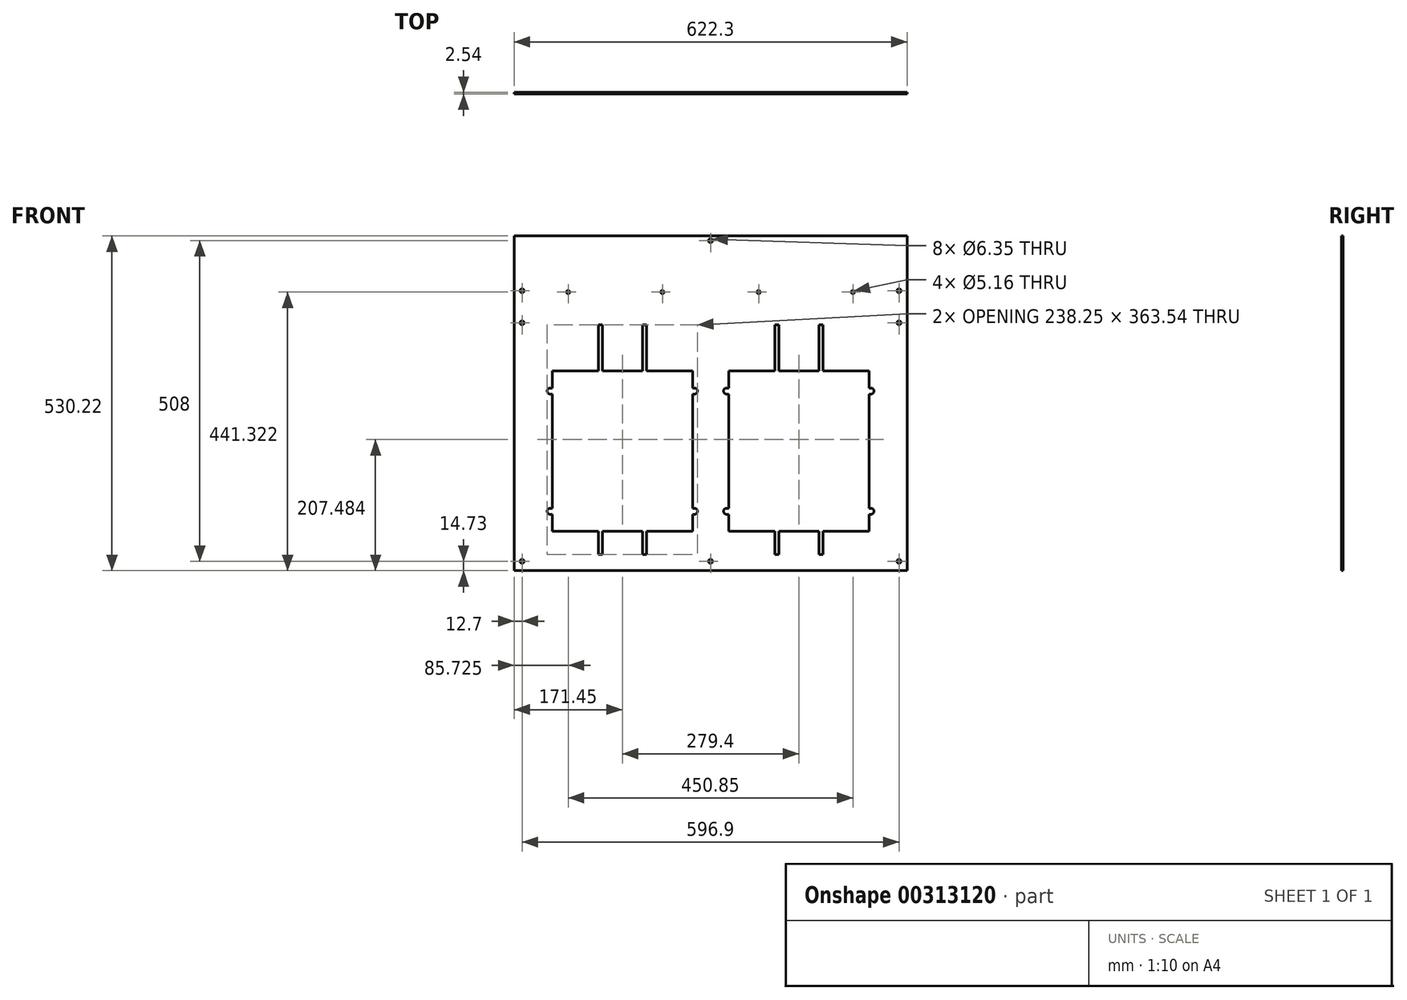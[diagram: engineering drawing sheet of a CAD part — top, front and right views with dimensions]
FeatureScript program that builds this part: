
annotation { "Feature Type Name" : "Feature", "Feature Type Description" : "" }
export const myFeature = defineFeature(function(context is Context, id is Id, definition is map)
    precondition{}
    {
        {
            var Q0;
            Q0=qCreatedBy(makeId("Front.planeOp"),FACE);
            var sketch = newSketch(context, id + "F0", { "sketchPlane" : qUnion([Q0])});
            skLineSegment(sketch, "E0.bottom", {"start": v(-311.15, 265.11) * mm, "end": v(311.15, 265.11) * mm});
            skLineSegment(sketch, "E0.top", {"start": v(-311.15, -265.11) * mm, "end": v(311.15, -265.11) * mm});
            skLineSegment(sketch, "E0.left", {"start": v(-311.15, 265.11) * mm, "end": v(-311.15, -265.11) * mm});
            skLineSegment(sketch, "E0.right", {"start": v(311.15, 265.11) * mm, "end": v(311.15, -265.11) * mm});
            skLineSegment(sketch, "E1.bottom", {"start": v(-250.83, 51.12) * mm, "end": v(-28.57, 51.12) * mm});
            skLineSegment(sketch, "E1.top", {"start": v(-250.82, -202.88) * mm, "end": v(-28.57, -202.88) * mm});
            skLineSegment(sketch, "E1.left", {"start": v(-250.82, 51.12) * mm, "end": v(-250.82, 24.2) * mm});
            skLineSegment(sketch, "E1.right", {"start": v(-28.57, 51.12) * mm, "end": v(-28.57, 24.2) * mm});
            skPoint(sketch, "E1.middle", {"position": v(-139.7, -75.88) * mm});
            skLineSegment(sketch, "E2", {"start": v(0, -75.88) * mm, "end": v(0, 0) * mm, "construction": true});
            skLineSegment(sketch, "E3", {"start": v(-139.7, -75.88) * mm, "end": v(0, -75.88) * mm, "construction": true});
            skArc(sketch, "E4", {"start": v(-254, 24.2) * mm, "mid": v(-258.83, 19.37) * mm, "end": v(-254, 14.54) * mm});
            skArc(sketch, "E5", {"start": v(-25.4, 14.54) * mm, "mid": v(-20.57, 19.37) * mm, "end": v(-25.4, 24.2) * mm});
            skArc(sketch, "E6", {"start": v(-25.4, -175.96) * mm, "mid": v(-20.57, -171.13) * mm, "end": v(-25.4, -166.3) * mm});
            skArc(sketch, "E7", {"start": v(-254, -166.3) * mm, "mid": v(-258.83, -171.13) * mm, "end": v(-254, -175.96) * mm});
            skLineSegment(sketch, "E8", {"start": v(-25.4, 24.2) * mm, "end": v(-28.58, 24.2) * mm});
            skLineSegment(sketch, "E9", {"start": v(-25.4, 14.54) * mm, "end": v(-28.57, 14.54) * mm});
            skLineSegment(sketch, "E10.trimOffspring", {"start": v(-28.57, 14.54) * mm, "end": v(-28.57, -166.3) * mm});
            skLineSegment(sketch, "E11", {"start": v(-25.4, -166.3) * mm, "end": v(-28.57, -166.3) * mm});
            skLineSegment(sketch, "E12", {"start": v(-25.4, -175.96) * mm, "end": v(-28.57, -175.96) * mm});
            skLineSegment(sketch, "E13.trimOffspring", {"start": v(-28.57, -175.96) * mm, "end": v(-28.57, -202.88) * mm});
            skLineSegment(sketch, "E14", {"start": v(-254, -166.3) * mm, "end": v(-250.82, -166.3) * mm});
            skLineSegment(sketch, "E15", {"start": v(-254, -175.96) * mm, "end": v(-250.82, -175.96) * mm});
            skLineSegment(sketch, "E16", {"start": v(-254, 24.2) * mm, "end": v(-250.82, 24.2) * mm});
            skLineSegment(sketch, "E17", {"start": v(-254, 14.54) * mm, "end": v(-250.82, 14.54) * mm});
            skLineSegment(sketch, "E18.trimOffspring", {"start": v(-250.82, 14.54) * mm, "end": v(-250.82, -166.3) * mm});
            skLineSegment(sketch, "E19.trimOffspring", {"start": v(-250.82, -175.96) * mm, "end": v(-250.82, -202.88) * mm});
            skLineSegment(sketch, "E20.1.0.0", {"start": v(28.57, -175.96) * mm, "end": v(28.57, -202.88) * mm});
            skLineSegment(sketch, "E20.1.0.1", {"start": v(250.82, 14.54) * mm, "end": v(250.82, -166.3) * mm});
            skLineSegment(sketch, "E20.1.0.2", {"start": v(139.7, -75.88) * mm, "end": v(279.4, -75.88) * mm, "construction": true});
            skLineSegment(sketch, "E20.1.0.3", {"start": v(250.82, 51.12) * mm, "end": v(250.82, 24.2) * mm});
            skLineSegment(sketch, "E20.1.0.4", {"start": v(250.82, -175.96) * mm, "end": v(250.82, -202.88) * mm});
            skPoint(sketch, "E20.1.0.5", {"position": v(139.7, -75.88) * mm});
            skLineSegment(sketch, "E20.1.0.6", {"start": v(28.57, 51.12) * mm, "end": v(250.82, 51.12) * mm});
            skLineSegment(sketch, "E20.1.0.7", {"start": v(28.57, -202.88) * mm, "end": v(250.82, -202.88) * mm});
            skLineSegment(sketch, "E20.1.0.8", {"start": v(28.57, 14.54) * mm, "end": v(28.57, -166.3) * mm});
            skLineSegment(sketch, "E20.1.0.9", {"start": v(28.57, 51.12) * mm, "end": v(28.57, 24.2) * mm});
            skLineSegment(sketch, "E20.1.0.10", {"start": v(25.4, -166.3) * mm, "end": v(28.57, -166.3) * mm});
            skLineSegment(sketch, "E20.1.0.11", {"start": v(25.4, 24.2) * mm, "end": v(28.58, 24.2) * mm});
            skArc(sketch, "E20.1.0.12", {"start": v(254, -175.96) * mm, "mid": v(258.83, -171.13) * mm, "end": v(254, -166.3) * mm});
            skLineSegment(sketch, "E20.1.0.13", {"start": v(254, -175.96) * mm, "end": v(250.82, -175.96) * mm});
            skLineSegment(sketch, "E20.1.0.14", {"start": v(25.4, -175.96) * mm, "end": v(28.57, -175.96) * mm});
            skLineSegment(sketch, "E20.1.0.15", {"start": v(254, -166.3) * mm, "end": v(250.82, -166.3) * mm});
            skArc(sketch, "E20.1.0.16", {"start": v(25.4, -166.3) * mm, "mid": v(20.57, -171.13) * mm, "end": v(25.4, -175.96) * mm});
            skLineSegment(sketch, "E20.1.0.17", {"start": v(254, 24.2) * mm, "end": v(250.82, 24.2) * mm});
            skLineSegment(sketch, "E20.1.0.18", {"start": v(254, 14.54) * mm, "end": v(250.82, 14.54) * mm});
            skArc(sketch, "E20.1.0.19", {"start": v(254, 14.54) * mm, "mid": v(258.83, 19.37) * mm, "end": v(254, 24.2) * mm});
            skLineSegment(sketch, "E20.1.0.20", {"start": v(25.4, 14.54) * mm, "end": v(28.57, 14.54) * mm});
            skArc(sketch, "E20.1.0.21", {"start": v(25.4, 24.2) * mm, "mid": v(20.57, 19.37) * mm, "end": v(25.4, 14.54) * mm});
            skLineSegment(sketch, "E20.direction1", {"start": v(-250.82, -202.88) * mm, "end": v(28.57, -202.88) * mm, "construction": true});
            skCircle(sketch, "E21", {"center": v(0, 257.62) * mm, "radius": 3.18 * mm});
            skCircle(sketch, "E22", {"center": v(-298.45, 178.24) * mm, "radius": 3.18 * mm});
            skCircle(sketch, "E23", {"center": v(-298.45, 127.44) * mm, "radius": 3.18 * mm});
            skCircle(sketch, "E24", {"center": v(-298.45, -250.38) * mm, "radius": 3.17 * mm});
            skCircle(sketch, "E25", {"center": v(298.45, 178.24) * mm, "radius": 3.18 * mm});
            skCircle(sketch, "E26", {"center": v(298.45, 127.44) * mm, "radius": 3.18 * mm});
            skCircle(sketch, "E27", {"center": v(298.45, -250.38) * mm, "radius": 3.18 * mm});
            skCircle(sketch, "E28", {"center": v(0, -250.38) * mm, "radius": 3.18 * mm});
            skPoint(sketch, "E28.centerSnap0", {"position": v(0, -265.11) * mm});
            skSolve(sketch);
        }
        {
            var Q0;
            Q0 = qSketchRegion(id + "F0", true);
            extrude(context, id + "F1", {"entities" : qUnion([Q0]), "endBound" : BoundingType.SYMMETRIC, "depth" : 2.54 * mm});
        }
        {
            var Q0;
            Q0=makeQuery(id+"F1.opExtrude","CAP_FACE",FACE,{"disambiguationData":[OSD([sQuery(id+"F0.wireOp",EDGE,"E0.bottom"),sQuery(id+"F0.wireOp",EDGE,"E0.top"),sQuery(id+"F0.wireOp",EDGE,"E0.left"),sQuery(id+"F0.wireOp",EDGE,"E0.right"),sQuery(id+"F0.wireOp",EDGE,"E1.bottom"),sQuery(id+"F0.wireOp",EDGE,"E1.top"),sQuery(id+"F0.wireOp",EDGE,"E1.left"),sQuery(id+"F0.wireOp",EDGE,"E1.right"),sQuery(id+"F0.wireOp",EDGE,"E4"),sQuery(id+"F0.wireOp",EDGE,"E5"),sQuery(id+"F0.wireOp",EDGE,"E6"),sQuery(id+"F0.wireOp",EDGE,"E7"),sQuery(id+"F0.wireOp",EDGE,"E8"),sQuery(id+"F0.wireOp",EDGE,"E9"),sQuery(id+"F0.wireOp",EDGE,"E10.trimOffspring"),sQuery(id+"F0.wireOp",EDGE,"E11"),sQuery(id+"F0.wireOp",EDGE,"E12"),sQuery(id+"F0.wireOp",EDGE,"E13.trimOffspring"),sQuery(id+"F0.wireOp",EDGE,"E14"),sQuery(id+"F0.wireOp",EDGE,"E15"),sQuery(id+"F0.wireOp",EDGE,"E16"),sQuery(id+"F0.wireOp",EDGE,"E17"),sQuery(id+"F0.wireOp",EDGE,"E18.trimOffspring"),sQuery(id+"F0.wireOp",EDGE,"E19.trimOffspring"),sQuery(id+"F0.wireOp",EDGE,"E20.1.0.0"),sQuery(id+"F0.wireOp",EDGE,"E20.1.0.1"),sQuery(id+"F0.wireOp",EDGE,"E20.1.0.3"),sQuery(id+"F0.wireOp",EDGE,"E20.1.0.4"),sQuery(id+"F0.wireOp",EDGE,"E20.1.0.6"),sQuery(id+"F0.wireOp",EDGE,"E20.1.0.7"),sQuery(id+"F0.wireOp",EDGE,"E20.1.0.8"),sQuery(id+"F0.wireOp",EDGE,"E20.1.0.9"),sQuery(id+"F0.wireOp",EDGE,"E20.1.0.10"),sQuery(id+"F0.wireOp",EDGE,"E20.1.0.11"),sQuery(id+"F0.wireOp",EDGE,"E20.1.0.12"),sQuery(id+"F0.wireOp",EDGE,"E20.1.0.13"),sQuery(id+"F0.wireOp",EDGE,"E20.1.0.14"),sQuery(id+"F0.wireOp",EDGE,"E20.1.0.15"),sQuery(id+"F0.wireOp",EDGE,"E20.1.0.16"),sQuery(id+"F0.wireOp",EDGE,"E20.1.0.17"),sQuery(id+"F0.wireOp",EDGE,"E20.1.0.18"),sQuery(id+"F0.wireOp",EDGE,"E20.1.0.19"),sQuery(id+"F0.wireOp",EDGE,"E20.1.0.20"),sQuery(id+"F0.wireOp",EDGE,"E20.1.0.21"),sQuery(id+"F0.wireOp",EDGE,"E21"),sQuery(id+"F0.wireOp",EDGE,"E22"),sQuery(id+"F0.wireOp",EDGE,"E23"),sQuery(id+"F0.wireOp",EDGE,"E24"),sQuery(id+"F0.wireOp",EDGE,"E25"),sQuery(id+"F0.wireOp",EDGE,"E26"),sQuery(id+"F0.wireOp",EDGE,"E27"),sQuery(id+"F0.wireOp",EDGE,"E28")])],"isStart":false});
            var sketch = newSketch(context, id + "F2", { "sketchPlane" : qUnion([Q0])});
            skLineSegment(sketch, "E29.bottom", {"start": v(-177.8, 51.12) * mm, "end": v(-171.45, 51.12) * mm});
            skLineSegment(sketch, "E29.top", {"start": v(-177.8, 124.14) * mm, "end": v(-171.45, 124.14) * mm});
            skLineSegment(sketch, "E29.left", {"start": v(-177.8, 51.12) * mm, "end": v(-177.8, 124.14) * mm});
            skLineSegment(sketch, "E29.right", {"start": v(-171.45, 51.12) * mm, "end": v(-171.45, 124.14) * mm});
            skLineSegment(sketch, "E30.bottom", {"start": v(-107.95, 51.12) * mm, "end": v(-101.6, 51.12) * mm});
            skLineSegment(sketch, "E30.top", {"start": v(-107.95, 124.14) * mm, "end": v(-101.6, 124.14) * mm});
            skLineSegment(sketch, "E30.left", {"start": v(-107.95, 51.12) * mm, "end": v(-107.95, 124.14) * mm});
            skLineSegment(sketch, "E30.right", {"start": v(-101.6, 51.12) * mm, "end": v(-101.6, 124.14) * mm});
            skLineSegment(sketch, "E31.bottom", {"start": v(-107.95, -202.88) * mm, "end": v(-101.6, -202.88) * mm});
            skLineSegment(sketch, "E31.top", {"start": v(-107.95, -239.4) * mm, "end": v(-101.6, -239.4) * mm});
            skLineSegment(sketch, "E31.left", {"start": v(-107.95, -202.88) * mm, "end": v(-107.95, -239.4) * mm});
            skLineSegment(sketch, "E31.right", {"start": v(-101.6, -202.88) * mm, "end": v(-101.6, -239.4) * mm});
            skLineSegment(sketch, "E32.bottom", {"start": v(-171.45, -202.88) * mm, "end": v(-177.8, -202.88) * mm});
            skLineSegment(sketch, "E32.top", {"start": v(-171.45, -239.4) * mm, "end": v(-177.8, -239.4) * mm});
            skLineSegment(sketch, "E32.left", {"start": v(-171.45, -202.88) * mm, "end": v(-171.45, -239.4) * mm});
            skLineSegment(sketch, "E32.right", {"start": v(-177.8, -202.88) * mm, "end": v(-177.8, -239.4) * mm});
            skLineSegment(sketch, "E33.1.0.0", {"start": v(101.6, 51.12) * mm, "end": v(101.6, 124.14) * mm});
            skLineSegment(sketch, "E33.1.0.1", {"start": v(107.95, 51.12) * mm, "end": v(107.95, 124.14) * mm});
            skLineSegment(sketch, "E33.1.0.2", {"start": v(171.45, -202.88) * mm, "end": v(171.45, -239.4) * mm});
            skLineSegment(sketch, "E33.1.0.3", {"start": v(177.8, -202.88) * mm, "end": v(177.8, -239.4) * mm});
            skLineSegment(sketch, "E33.1.0.4", {"start": v(171.45, 51.12) * mm, "end": v(171.45, 124.14) * mm});
            skLineSegment(sketch, "E33.1.0.5", {"start": v(177.8, 51.12) * mm, "end": v(177.8, 124.14) * mm});
            skLineSegment(sketch, "E33.1.0.6", {"start": v(101.6, -202.88) * mm, "end": v(101.6, -239.4) * mm});
            skLineSegment(sketch, "E33.1.0.7", {"start": v(107.95, -202.88) * mm, "end": v(107.95, -239.4) * mm});
            skLineSegment(sketch, "E33.1.0.8", {"start": v(171.45, -239.4) * mm, "end": v(177.8, -239.4) * mm});
            skLineSegment(sketch, "E33.1.0.9", {"start": v(101.6, 124.14) * mm, "end": v(107.95, 124.14) * mm});
            skLineSegment(sketch, "E33.1.0.10", {"start": v(107.95, -202.88) * mm, "end": v(101.6, -202.88) * mm});
            skLineSegment(sketch, "E33.1.0.11", {"start": v(101.6, 51.12) * mm, "end": v(107.95, 51.12) * mm});
            skLineSegment(sketch, "E33.1.0.12", {"start": v(171.45, 51.12) * mm, "end": v(177.8, 51.12) * mm});
            skLineSegment(sketch, "E33.1.0.13", {"start": v(171.45, 124.14) * mm, "end": v(177.8, 124.14) * mm});
            skLineSegment(sketch, "E33.1.0.14", {"start": v(171.45, -202.88) * mm, "end": v(177.8, -202.88) * mm});
            skLineSegment(sketch, "E33.1.0.15", {"start": v(107.95, -239.4) * mm, "end": v(101.6, -239.4) * mm});
            skLineSegment(sketch, "E33.direction1", {"start": v(-177.8, -239.4) * mm, "end": v(101.6, -239.4) * mm, "construction": true});
            skPoint(sketch, "E34", {"position": v(-104.77, 51.12) * mm});
            skPoint(sketch, "E35", {"position": v(-174.62, 51.12) * mm});
            skCircle(sketch, "E36", {"center": v(225.42, 176.21) * mm, "radius": 2.58 * mm});
            skCircle(sketch, "E37", {"center": v(-225.42, 176.21) * mm, "radius": 2.58 * mm});
            skLineSegment(sketch, "E38", {"start": v(225.42, 176.21) * mm, "end": v(-225.42, 176.21) * mm, "construction": true});
            skPoint(sketch, "E39", {"position": v(0, 176.21) * mm});
            skCircle(sketch, "E40", {"center": v(76.2, 176.21) * mm, "radius": 2.58 * mm});
            skCircle(sketch, "E41", {"center": v(-76.2, 176.21) * mm, "radius": 2.58 * mm});
            skLineSegment(sketch, "E42.direction1", {"start": v(-225.42, 176.21) * mm, "end": v(-76.2, 176.21) * mm, "construction": true});
            skLineSegment(sketch, "E43.direction1", {"start": v(-225.43, 176.21) * mm, "end": v(0, 176.21) * mm, "construction": true});
            skSolve(sketch);
        }
        {
            var Q0;
            Q0 = qSketchRegion(id + "F2", true);
            extrude(context, id + "F3", {"entities" : qUnion([Q0]), "operationType" : NewBodyOperationType.REMOVE, "endBound" : BoundingType.THROUGH_ALL, "oppositeDirection" : true, "depth" : 25.4 * mm});
        }
    });
